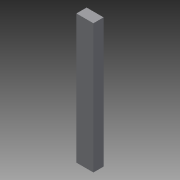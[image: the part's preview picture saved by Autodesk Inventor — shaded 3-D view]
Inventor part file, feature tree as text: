
AUTODESK INVENTOR PART (.ipt)
format: ipt  version: 2013 (Build 170138000, 138)  size: 68,096 bytes
history: native  units: in
note: dims shown in document units (in); Inventor stores cm internally (conversion verified against a paired STEP export)
features: extrude x1, sketch x1
ambient origin geometry x8: Origin, YZ Plane, XZ Plane, XY Plane, X Axis, Y Axis, Z Axis, Center Point
bodies: Solid1 (feature_tree)
feature tree (2):
  extrude  "Extrusion1"  Depth=3.0in
  sketch  "Sketch1"  dims[d0=5.0in d1=3.0in d2=5.0in d3=38.0in d4=3.0in d5=0.0in]
